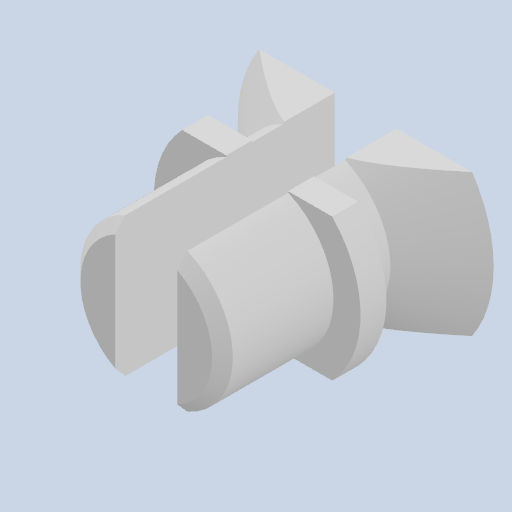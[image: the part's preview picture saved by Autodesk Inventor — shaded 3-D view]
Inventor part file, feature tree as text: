
AUTODESK INVENTOR PART (.ipt)
format: ipt  version: 2022 (Build 260153000, 153)  size: 167,424 bytes
history: native  units: mm
features: reference x6, other x6, sketch x2, revolve x1, extrude x1
ambient origin geometry x8: Origin, YZ Plane, XZ Plane, XY Plane, X Axis, Y Axis, Z Axis, Center Point
bodies: Body1 (feature_tree)
feature tree (16):
  revolve  "Вращение1"
  extrude  "Выдавливание3"  Depth=5.9mm
  sketch  "Эскиз1"
  reference  "Ссылка9"
  reference  "Ссылка10"
  reference  "Ссылка11"
  reference  "Ссылка12"
  reference  "Ссылка13"
  reference  "Ссылка14"
  sketch  "Эскиз3"
  other  "<userpath>\Documents\Git\MZCAT_2024\MZCAT_4.iam"
  other  "MZCAT_4.iam"
  other  "base plate:1"
  other  "parasit_gear:1"
  other  "shelka_lidar:2"
  other  "middle_gear_fixator:1"
